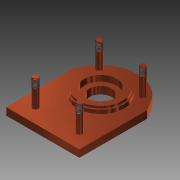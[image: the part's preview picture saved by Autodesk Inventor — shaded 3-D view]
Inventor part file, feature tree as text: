
AUTODESK INVENTOR PART (.ipt)
format: ipt  version: 2015 (Build 190159000, 159)  size: 168,960 bytes
history: native  units: mm
features: extrude x5, sketch x5, thread x4, chamfer x1
ambient origin geometry x8: Origin, YZ Plane, XZ Plane, XY Plane, X Axis, Y Axis, Z Axis, Center Point
bodies: 实体1 (feature_tree)
feature tree (15):
  extrude  "拉伸1"  Depth=39.5mm
  extrude  "拉伸2"  TaperAngle=60.0deg  [1 undecoded]
  extrude  "拉伸3"  Depth=5.0mm
  extrude  "拉伸4"  Depth=4.0mm TaperAngle=0.0deg
  extrude  "拉伸5"  Depth=2.0mm
  thread  "螺纹1"  [1 undecoded]
  thread  "螺纹2"  [1 undecoded]
  thread  "螺纹3"  [1 undecoded]
  thread  "螺纹4"  [1 undecoded]
  chamfer  "倒角1"  Distance=4.0mm
  sketch  "草图1"  dims[d0=50.0mm d1=39.5mm]
  sketch  "草图2"  dims[d2=13.701357mm d3=60.0deg]
  sketch  "草图3"  dims[d4=5.0mm d5=0.0mm d6=32.0mm]
  sketch  "草图4"  dims[d7=22.0mm d8=4.0mm d9=0.0mm]
  sketch  "草图5"  dims[d10=32.0mm d11=30.0mm d12=1.5mm d13=0.0mm d14=15.0mm d15=1.5mm d16=0.0mm d17=4.0mm d18=4.0mm d19=4.0mm d20=4.0mm d21=10.0mm d22=10.0mm d23=10.0mm d24=10.0mm d25=20.5mm d26=10.0mm d27=10.0mm d28=18.0mm d29=0.0mm d30=6.0mm d31=0.0mm d32=6.0mm d33=0.0mm d34=6.0mm d35=0.0mm d36=6.0mm d37=0.0mm d38=0.25mm d39=2.0mm d40=45.0deg]
note: 5 required parameter values undecoded (feature->parameter linkage not recoverable at this tier; creation-order binding heuristic only, values carry confidence <= 0.55)
